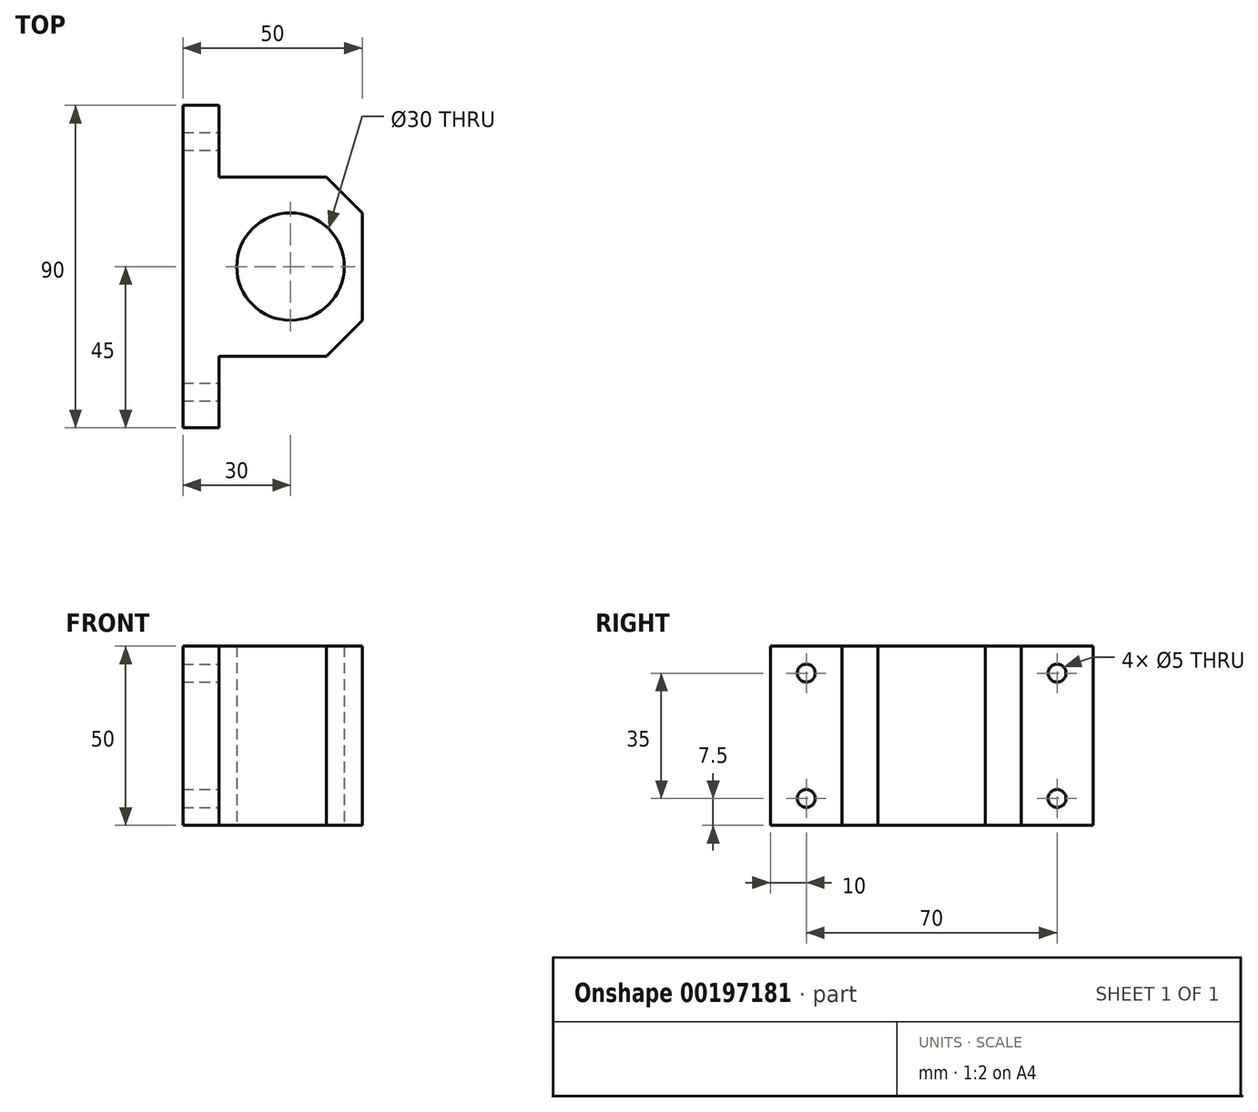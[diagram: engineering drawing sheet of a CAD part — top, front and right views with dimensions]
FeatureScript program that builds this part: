
annotation { "Feature Type Name" : "Feature", "Feature Type Description" : "" }
export const myFeature = defineFeature(function(context is Context, id is Id, definition is map)
    precondition{}
    {
        {
            var Q0;
            Q0=qCreatedBy(makeId("Top.planeOp"),FACE);
            var sketch = newSketch(context, id + "F0", { "sketchPlane" : qUnion([Q0])});
            skLineSegment(sketch, "E0", {"start": v(0, 45) * mm, "end": v(-10, 45) * mm});
            skLineSegment(sketch, "E1", {"start": v(-10, 45) * mm, "end": v(-10, -45) * mm});
            skLineSegment(sketch, "E2", {"start": v(-10, -45) * mm, "end": v(0, -45) * mm});
            skLineSegment(sketch, "E3", {"start": v(0, 0) * mm, "end": v(40, 0) * mm, "construction": true});
            skLineSegment(sketch, "E4", {"start": v(0, -25) * mm, "end": v(30, -25) * mm});
            skLineSegment(sketch, "E5", {"start": v(30, -25) * mm, "end": v(40, -15) * mm});
            skLineSegment(sketch, "E6", {"start": v(40, -15) * mm, "end": v(40, 15) * mm});
            skLineSegment(sketch, "E7", {"start": v(40, 15) * mm, "end": v(30, 25) * mm});
            skLineSegment(sketch, "E8", {"start": v(30, 25) * mm, "end": v(0, 25) * mm});
            skCircle(sketch, "E9", {"center": v(20, 0) * mm, "radius": 15 * mm});
            skLineSegment(sketch, "E10", {"start": v(0, -45) * mm, "end": v(0, -25) * mm});
            skLineSegment(sketch, "E11", {"start": v(0, 25) * mm, "end": v(0, 45) * mm});
            skSolve(sketch);
        }
        {
            var Q0;
            Q0 = qSketchRegion(id + "F0", true);
            extrude(context, id + "F1", {"entities" : qUnion([Q0]), "depth" : 50 * mm});
        }
        {
            var Q0;
            Q0=makeQuery(id+"F1.opExtrude","SWEPT_FACE",FACE,{"disambiguationData":[OSD([sQuery(id+"F0.wireOp",EDGE,"E10")])]});
            var sketch = newSketch(context, id + "F2", { "sketchPlane" : qUnion([Q0])});
            skLineSegment(sketch, "E12", {"start": v(0, 0) * mm, "end": v(0, 50) * mm, "construction": true});
            skLineSegment(sketch, "E13.bottom", {"start": v(-35, 42.5) * mm, "end": v(35, 42.5) * mm, "construction": true});
            skLineSegment(sketch, "E13.top", {"start": v(-35, 7.5) * mm, "end": v(35, 7.5) * mm, "construction": true});
            skLineSegment(sketch, "E13.left", {"start": v(-35, 42.5) * mm, "end": v(-35, 7.5) * mm, "construction": true});
            skLineSegment(sketch, "E13.right", {"start": v(35, 42.5) * mm, "end": v(35, 7.5) * mm, "construction": true});
            skPoint(sketch, "E13.middle", {"position": v(0, 25) * mm});
            skCircle(sketch, "E14", {"center": v(-35, 42.5) * mm, "radius": 2.5 * mm});
            skCircle(sketch, "E15", {"center": v(-35, 7.5) * mm, "radius": 2.5 * mm});
            skCircle(sketch, "E16", {"center": v(35, 7.5) * mm, "radius": 2.5 * mm});
            skCircle(sketch, "E17", {"center": v(35, 42.5) * mm, "radius": 2.5 * mm});
            skSolve(sketch);
        }
        {
            var Q0;
            Q0 = qSketchRegion(id + "F2", true);
            extrude(context, id + "F3", {"entities" : qUnion([Q0]), "operationType" : NewBodyOperationType.REMOVE, "oppositeDirection" : true, "depth" : 25 * mm});
        }
    });
